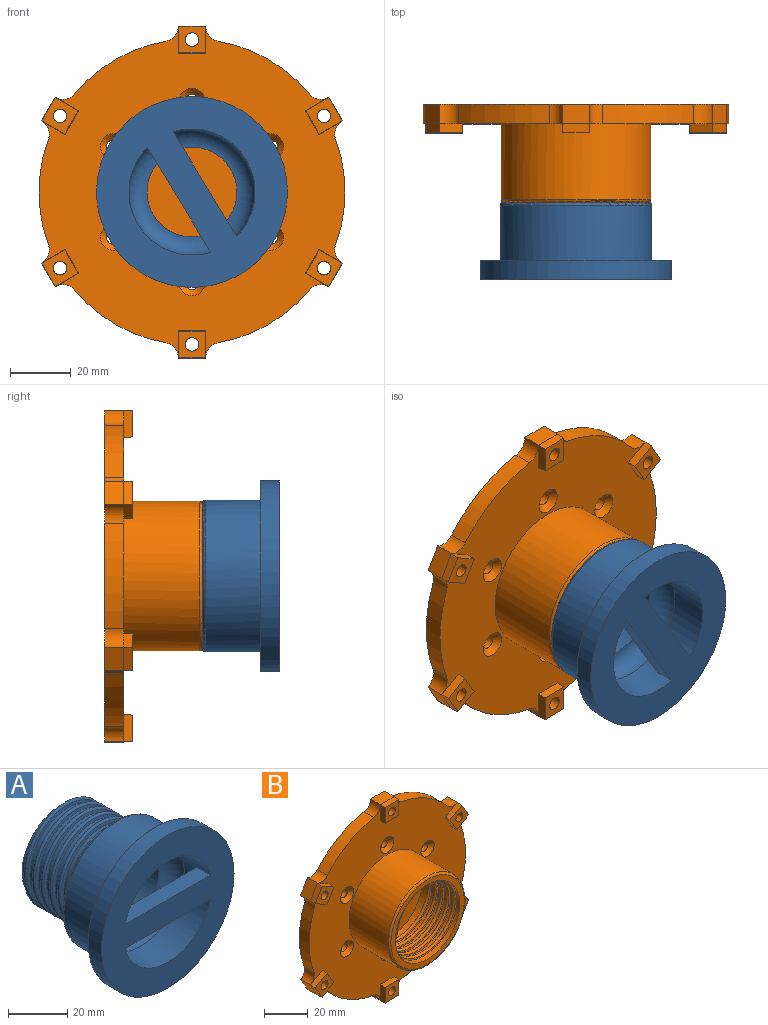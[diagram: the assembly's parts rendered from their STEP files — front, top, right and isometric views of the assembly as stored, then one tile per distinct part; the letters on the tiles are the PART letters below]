
ASSEMBLY  parts=2 mates=1
PART A: 25 faces, bbox 63.2x51x63.2 mm
  f0: cylinder r=20.83mm len=41.66mm, axis (0,-1,0), area 1579.6mm2, adj f6,f20,f21,f22,f23
  f1: plane 48.18x48.18mm, normal (0,1,0), area 723.2mm2, adj f2,f11,f12,f19,f24
  f2: bspline ~45.36x39.28mm, area 848.9mm2, adj f1,f10,f12,f14,f15,f16,f17,f18
  f3: bspline ~45.36x39.28mm, area 833.6mm2, adj f10,f11,f12,f13,f14,f15,f16,f17
  f4: cylinder r=31.5mm len=62.99mm, axis (0,-1,0), area 1256.6mm2, adj f5,f6
  f5: plane 62.99x62.99mm, normal (0,1,0), area 1153mm2, adj f4,f7
  f6: plane 62.99x62.99mm, normal (0,-1,0), area 2166.1mm2, adj f0,f4,f21,f22
  f7: cylinder r=25mm len=50mm, axis (0,-1,0), area 2835.3mm2, adj f5,f24
  f8: cylinder r=14.83mm len=31.75mm, axis (0,-1,0), area 2958.1mm2, adj f9,f23
  f9: plane 37x37mm, normal (0,1,0), area 384.5mm2, adj f8,f13
  f10: plane 1.9x1.85mm, normal (0,0,-1), area 2.4mm2, adj f2,f3,f12,f13
  f11: plane 1.89x1.56mm, normal (0,0,1), area 2mm2, adj f1,f3,f12,f19
  f12: bspline ~47.67x41.28mm, area 1462.2mm2, adj f1,f2,f3,f10,f11
  f13: cylinder r=18.5mm len=37mm, axis (0,1,0), area 234.2mm2, adj f3,f9,f10,f14
  f14: cylinder r=18.5mm len=37mm, axis (0,1,0), area 259.3mm2, adj f2,f3,f13,f15
  f15: cylinder r=18.5mm len=37mm, axis (0,1,0), area 259.2mm2, adj f2,f3,f14,f16
  f16: cylinder r=18.5mm len=37mm, axis (0,1,0), area 259.1mm2, adj f2,f3,f15,f17
  f17: cylinder r=18.5mm len=37mm, axis (0,1,0), area 259.4mm2, adj f2,f3,f16,f18
  f18: cylinder r=18.5mm len=37mm, axis (0,1,0), area 259.1mm2, adj f2,f3,f17,f19
  f19: cylinder r=18.5mm len=37mm, axis (0,1,0), area 189.9mm2, adj f1,f2,f11,f18
  f20: plane 41.66x10mm, normal (0,1,0), area 412.5mm2, adj f0,f21,f22
  f21: plane 40.44x6.35mm, normal (0,0,1), area 256.8mm2, adj f0,f6,f20
  f22: plane 40.44x6.35mm, normal (0,0,-1), area 256.8mm2, adj f0,f6,f20
  f23: torus R=14.83mm, axis (0,1,0), area 1104.3mm2, adj f0,f8
  f24: torus R=24mm, axis (0,1,0), area 243.2mm2, adj f1,f7
PART B: 102 faces, bbox 101x32.4x109.6 mm
  f0: cylinder r=20.83mm len=41.66mm, axis (0,1,0), area 595.5mm2, adj f1,f8,f19,f101
  f1: cylinder r=20.83mm len=41.66mm, axis (0,1,0), area 287.9mm2, adj f0,f2,f6,f8
  f2: cylinder r=20.83mm len=41.66mm, axis (0,1,0), area 287.9mm2, adj f1,f3,f6,f8
  f3: cylinder r=20.83mm len=41.66mm, axis (0,1,0), area 287.9mm2, adj f2,f4,f6,f8
  f4: cylinder r=20.83mm len=41.66mm, axis (0,1,0), area 287.9mm2, adj f3,f5,f6,f8
  f5: cylinder r=20.83mm len=41.66mm, axis (0,1,0), area 261.7mm2, adj f4,f6,f18,f99
  f6: bspline ~48.1x41.66mm, area 575.8mm2, adj f1,f2,f3,f4,f5,f7,f19,f99
  f7: bspline ~46.04x39.87mm, area 1418.6mm2, adj f6,f8,f19,f99
  f8: bspline ~48.1x41.66mm, area 576mm2, adj f0,f1,f2,f3,f4,f7,f19,f99
  f9: cylinder r=50.5mm len=34.67mm, axis (0,1,0), area 224.7mm2, adj f10,f16,f69,f78
  f10: plane 109.5x101mm, normal (0,-1,0), area 5551.3mm2, adj f9,f11,f12,f13,f14,f15,f17,f20
  f11: cylinder r=50.5mm len=30.02mm, axis (0,1,0), area 224.7mm2, adj f10,f16,f59,f68
  f12: cylinder r=50.5mm len=30.02mm, axis (0,1,0), area 224.7mm2, adj f10,f16,f49,f58
  f13: cylinder r=50.5mm len=34.67mm, axis (0,1,0), area 224.7mm2, adj f10,f16,f39,f48
  f14: cylinder r=50.5mm len=30.02mm, axis (0,1,0), area 224.7mm2, adj f10,f16,f29,f38
  f15: cylinder r=50.5mm len=30.02mm, axis (0,1,0), area 224.7mm2, adj f10,f16,f28,f79
  f16: plane 109.6x101mm, normal (0,1,0), area 8032.4mm2, adj f9,f11,f12,f13,f14,f15,f25,f26
  f17: cylinder r=24.7mm len=49.4mm, axis (0,1,0), area 3879.9mm2, adj f10,f80
  f18: plane 47.4x47.4mm, normal (0,-1,0), area 401.8mm2, adj f5,f80
  f19: plane 1.8x1.6mm, normal (0,0,1), area 2.4mm2, adj f0,f6,f7,f8
  f20: plane 9x3mm, normal (1,-0.03,0), area 26.7mm2, adj f10,f21,f23,f24,f25
  f21: plane 9x3mm, normal (0,-0.03,1), area 26.7mm2, adj f20,f22,f24,f27
  f22: plane 9x3mm, normal (-1,-0.03,0), area 26.7mm2, adj f10,f21,f23,f24,f26
  f23: plane 9x3mm, normal (0,-0.03,-1), area 26.7mm2, adj f10,f20,f22,f24
  f24: plane 8.79x8.79mm, normal (0,-1,0), area 61.4mm2, adj f20,f21,f22,f23,f81
  f25: plane 6.35x0.05mm, normal (1,0,0), area 0.3mm2, adj f16,f20,f27,f28
  f26: plane 6.35x0.05mm, normal (-1,0,0), area 0.3mm2, adj f16,f22,f27,f29
  f27: plane 9x6.35mm, normal (0,0,1), area 57.1mm2, adj f16,f21,f25,f26
  f28: cylinder r=5.08mm len=6.35mm, axis (0,1,0), area 45.1mm2, adj f10,f15,f16,f25
  f29: cylinder r=5.08mm len=6.35mm, axis (0,1,0), area 45.1mm2, adj f10,f14,f16,f26
  f30: plane 7.79x4.54mm, normal (0.5,-0.03,0.87), area 26.7mm2, adj f10,f31,f33,f34,f35
  f31: plane 7.79x4.54mm, normal (-0.87,-0.03,0.5), area 26.7mm2, adj f30,f32,f34,f37
  f32: plane 7.79x4.54mm, normal (-0.5,-0.03,-0.87), area 26.7mm2, adj f10,f31,f33,f34,f36
  f33: plane 7.79x4.54mm, normal (0.87,-0.03,-0.5), area 26.7mm2, adj f10,f30,f32,f34
  f34: plane 12.01x12.01mm, normal (0,-1,0), area 61.4mm2, adj f30,f31,f32,f33,f84
  f35: plane 6.35x0.04mm, normal (0.5,0,0.87), area 0.3mm2, adj f16,f30,f37,f38
  f36: plane 6.35x0.04mm, normal (-0.5,0,-0.87), area 0.3mm2, adj f16,f32,f37,f39
  f37: plane 7.79x6.35mm, normal (-0.87,0,0.5), area 57.2mm2, adj f16,f31,f35,f36
  f38: cylinder r=5.08mm len=6.44mm, axis (0,1,0), area 45.1mm2, adj f10,f14,f16,f35
  f39: cylinder r=5.08mm len=6.35mm, axis (0,1,0), area 45.1mm2, adj f10,f13,f16,f36
  f40: plane 7.79x4.54mm, normal (-0.5,-0.03,0.87), area 26.7mm2, adj f10,f41,f43,f44,f45
  f41: plane 7.79x4.54mm, normal (-0.87,-0.03,-0.5), area 26.7mm2, adj f40,f42,f44,f47
  f42: plane 7.79x4.54mm, normal (0.5,-0.03,-0.87), area 26.7mm2, adj f10,f41,f43,f44,f46
  f43: plane 7.79x4.54mm, normal (0.87,-0.03,0.5), area 26.7mm2, adj f10,f40,f42,f44
  f44: plane 12.01x12.01mm, normal (0,-1,0), area 61.4mm2, adj f40,f41,f42,f43,f87
  f45: plane 6.35x0.04mm, normal (-0.5,0,0.87), area 0.3mm2, adj f16,f40,f47,f48
  f46: plane 6.35x0.04mm, normal (0.5,0,-0.87), area 0.3mm2, adj f16,f42,f47,f49
  f47: plane 7.79x6.35mm, normal (-0.87,0,-0.5), area 57.2mm2, adj f16,f41,f45,f46
  f48: cylinder r=5.08mm len=6.35mm, axis (0,1,0), area 45.1mm2, adj f10,f13,f16,f45
  f49: cylinder r=5.08mm len=6.44mm, axis (0,1,0), area 45.1mm2, adj f10,f12,f16,f46
  f50: plane 9x3mm, normal (-1,-0.03,0), area 26.7mm2, adj f10,f51,f53,f54,f55
  f51: plane 9x3mm, normal (0,-0.03,-1), area 26.7mm2, adj f50,f52,f54,f57
  f52: plane 9x3mm, normal (1,-0.03,0), area 26.7mm2, adj f10,f51,f53,f54,f56
  f53: plane 9x3mm, normal (0,-0.03,1), area 26.7mm2, adj f10,f50,f52,f54
  f54: plane 8.79x8.79mm, normal (0,-1,0), area 61.4mm2, adj f50,f51,f52,f53,f90
  f55: plane 6.35x0.05mm, normal (-1,0,0), area 0.3mm2, adj f16,f50,f57,f58
  f56: plane 6.35x0.05mm, normal (1,0,0), area 0.3mm2, adj f16,f52,f57,f59
  f57: plane 9x6.35mm, normal (0,0,-1), area 57.1mm2, adj f16,f51,f55,f56
  f58: cylinder r=5.08mm len=6.35mm, axis (0,1,0), area 45.1mm2, adj f10,f12,f16,f55
  f59: cylinder r=5.08mm len=6.35mm, axis (0,1,0), area 45.1mm2, adj f10,f11,f16,f56
  f60: plane 7.79x4.54mm, normal (-0.5,-0.03,-0.87), area 26.7mm2, adj f10,f61,f63,f64,f65
  f61: plane 7.79x4.54mm, normal (0.87,-0.03,-0.5), area 26.7mm2, adj f60,f62,f64,f67
  f62: plane 7.79x4.54mm, normal (0.5,-0.03,0.87), area 26.7mm2, adj f10,f61,f63,f64,f66
  f63: plane 7.79x4.54mm, normal (-0.87,-0.03,0.5), area 26.7mm2, adj f10,f60,f62,f64
  f64: plane 12.01x12.01mm, normal (0,-1,0), area 61.4mm2, adj f60,f61,f62,f63,f93
  f65: plane 6.35x0.04mm, normal (-0.5,0,-0.87), area 0.3mm2, adj f16,f60,f67,f68
  f66: plane 6.35x0.04mm, normal (0.5,0,0.87), area 0.3mm2, adj f16,f62,f67,f69
  f67: plane 7.79x6.35mm, normal (0.87,0,-0.5), area 57.2mm2, adj f16,f61,f65,f66
  f68: cylinder r=5.08mm len=6.44mm, axis (0,1,0), area 45.1mm2, adj f10,f11,f16,f65
  f69: cylinder r=5.08mm len=6.35mm, axis (0,1,0), area 45.1mm2, adj f9,f10,f16,f66
  f70: plane 7.79x4.54mm, normal (0.5,-0.03,-0.87), area 26.7mm2, adj f10,f71,f73,f74,f75
  f71: plane 7.79x4.54mm, normal (0.87,-0.03,0.5), area 26.7mm2, adj f70,f72,f74,f77
  f72: plane 7.79x4.54mm, normal (-0.5,-0.03,0.87), area 26.7mm2, adj f10,f71,f73,f74,f76
  f73: plane 7.79x4.54mm, normal (-0.87,-0.03,-0.5), area 26.7mm2, adj f10,f70,f72,f74
  f74: plane 12.01x12.01mm, normal (0,-1,0), area 61.4mm2, adj f70,f71,f72,f73,f96
  f75: plane 6.35x0.04mm, normal (0.5,0,-0.87), area 0.3mm2, adj f16,f70,f77,f78
  f76: plane 6.35x0.04mm, normal (-0.5,0,0.87), area 0.3mm2, adj f16,f72,f77,f79
  f77: plane 7.79x6.35mm, normal (0.87,0,0.5), area 57.2mm2, adj f16,f71,f75,f76
  f78: cylinder r=5.08mm len=6.35mm, axis (0,1,0), area 45.1mm2, adj f9,f10,f16,f75
  f79: cylinder r=5.08mm len=6.44mm, axis (0,1,0), area 45.1mm2, adj f10,f15,f16,f76
  f80: torus R=23.7mm, axis (0,-1,0), area 240.2mm2, adj f17,f18
  f81: cylinder r=2.25mm len=9.35mm, axis (0,-1,0), area 132.2mm2, adj f16,f24
  f82: cylinder r=2.25mm len=4.5mm, axis (0,-1,0), area 61.5mm2, adj f16,f83
  f83: cone r=2.25mm half-angle=45deg, axis (0,-1,0), area 57.8mm2, adj f10,f82
  f84: cylinder r=2.25mm len=9.35mm, axis (0,-1,0), area 132.2mm2, adj f16,f34
  f85: cylinder r=2.25mm len=4.5mm, axis (0,-1,0), area 61.5mm2, adj f16,f86
  f86: cone r=2.25mm half-angle=45deg, axis (0,-1,0), area 57.8mm2, adj f10,f85
  f87: cylinder r=2.25mm len=9.35mm, axis (0,-1,0), area 132.2mm2, adj f16,f44
  f88: cylinder r=2.25mm len=4.5mm, axis (0,-1,0), area 61.5mm2, adj f16,f89
  f89: cone r=2.25mm half-angle=45deg, axis (0,-1,0), area 57.8mm2, adj f10,f88
  f90: cylinder r=2.25mm len=9.35mm, axis (0,-1,0), area 132.2mm2, adj f16,f54
  f91: cylinder r=2.25mm len=4.5mm, axis (0,-1,0), area 61.5mm2, adj f16,f92
  f92: cone r=2.25mm half-angle=45deg, axis (0,-1,0), area 57.8mm2, adj f10,f91
  f93: cylinder r=2.25mm len=9.35mm, axis (0,-1,0), area 132.2mm2, adj f16,f64
  f94: cylinder r=2.25mm len=4.5mm, axis (0,-1,0), area 61.5mm2, adj f16,f95
  f95: cone r=2.25mm half-angle=45deg, axis (0,-1,0), area 57.8mm2, adj f10,f94
  f96: cylinder r=2.25mm len=9.35mm, axis (0,-1,0), area 132.2mm2, adj f16,f74
  f97: cylinder r=2.25mm len=4.5mm, axis (0,-1,0), area 61.5mm2, adj f16,f98
  f98: cone r=2.25mm half-angle=45deg, axis (0,-1,0), area 57.8mm2, adj f10,f97
  f99: plane 2.35x1.83mm, normal (0.8,0,-0.6), area 4.2mm2, adj f5,f6,f7,f8
  f100: cylinder r=4.76mm len=9.53mm, axis (0,1,0), area 239.4mm2, adj f16,f101
  f101: plane 41.66x41.66mm, normal (0,-1,0), area 1291.6mm2, adj f0,f100
PLACE A rot(axis=(0,-1,0),121.1deg) t=(0,-57.75,0)mm
PLACE B at identity fixed
MATE revolute A.f0 <-> B.f0  axis (0,-1,0) through (0,-57.75,0)mm
